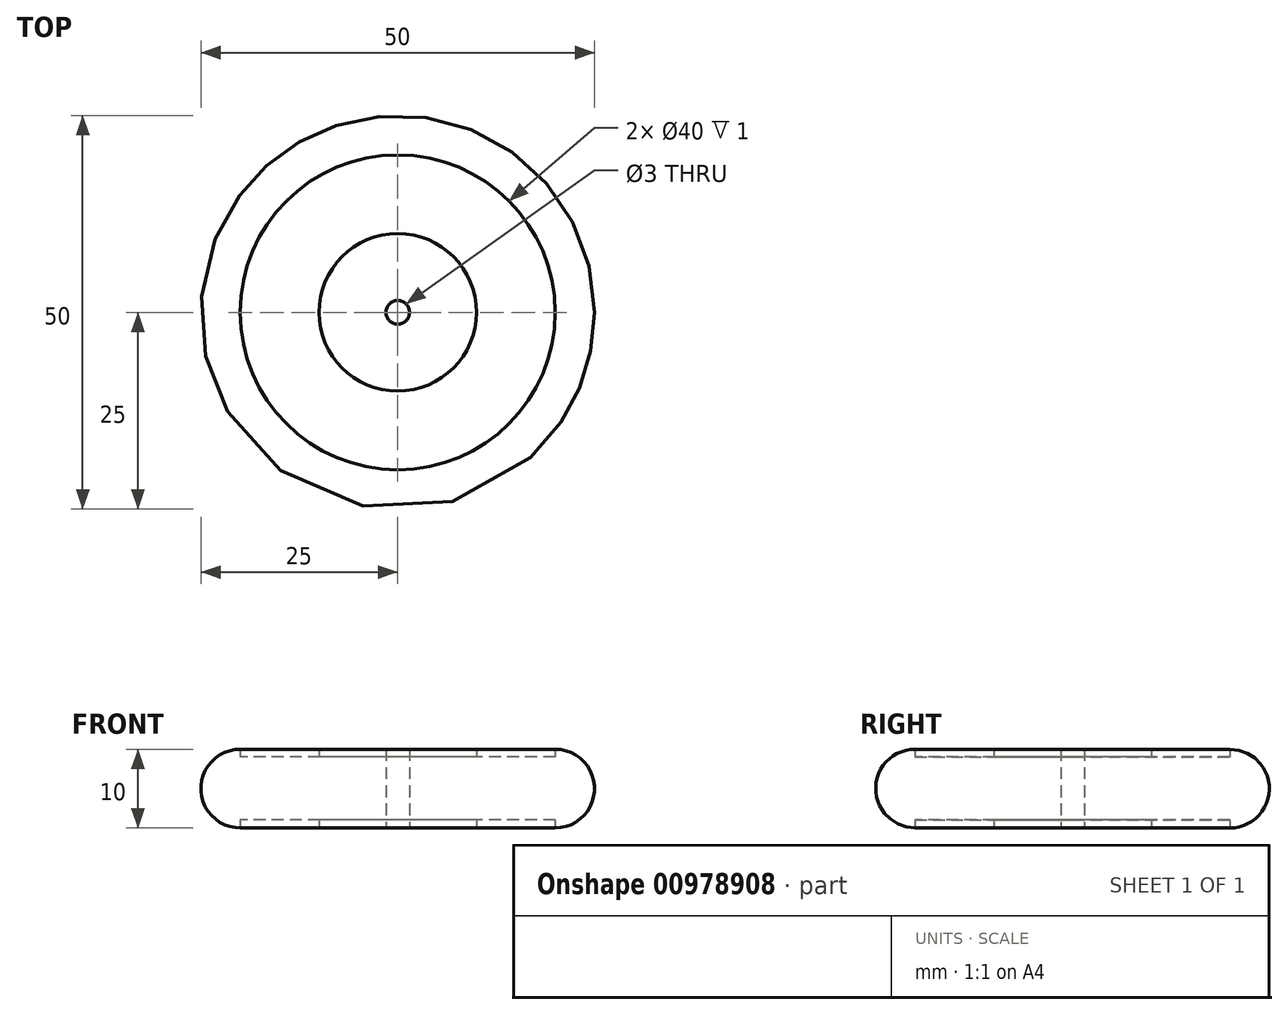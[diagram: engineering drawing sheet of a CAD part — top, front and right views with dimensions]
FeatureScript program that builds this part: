
annotation { "Feature Type Name" : "Feature", "Feature Type Description" : "" }
export const myFeature = defineFeature(function(context is Context, id is Id, definition is map)
    precondition{}
    {
        {
            var Q0;
            Q0=qCreatedBy(makeId("Top.planeOp"),FACE);
            var sketch = newSketch(context, id + "F0", { "sketchPlane" : qUnion([Q0])});
            skCircle(sketch, "E0", {"center": v(0, 0) * mm, "radius": 10 * mm});
            skCircle(sketch, "E1", {"center": v(0, 0) * mm, "radius": 20 * mm});
            skCircle(sketch, "E2", {"center": v(0, 0) * mm, "radius": 25 * mm});
            skSolve(sketch);
        }
        {
            var Q0;
            Q0=makeQuery(id+"F0.imprint","IMPRINT",FACE,{"disambiguationData":[TD([[makeQuery(id+"F0.imprint","IMPRINT",EDGE,{"derivedFrom":sQuery(id+"F0.wireOp",EDGE,"E1")}),-1.0]])]});
            var Q1;
            Q1=makeQuery(id+"F0.imprint","IMPRINT",FACE,{"disambiguationData":[TD([[makeQuery(id+"F0.imprint","IMPRINT",EDGE,{"derivedFrom":sQuery(id+"F0.wireOp",EDGE,"E0")}),1.0]])]});
            extrude(context, id + "F1", {"entities" : qUnion([Q0, Q1]), "endBound" : BoundingType.SYMMETRIC, "depth" : 10 * mm, "offsetDistance" : 25 * mm});
        }
        {
            var Q0;
            Q0=makeQuery(id+"F0.imprint","IMPRINT",FACE,{"disambiguationData":[TD([[makeQuery(id+"F0.imprint","IMPRINT",EDGE,{"derivedFrom":sQuery(id+"F0.wireOp",EDGE,"E0")}),-1.0]])]});
            extrude(context, id + "F2", {"entities" : qUnion([Q0]), "operationType" : NewBodyOperationType.ADD, "endBound" : BoundingType.SYMMETRIC, "depth" : 8 * mm, "offsetDistance" : 25 * mm});
        }
        {
            var Q0;
            Q0=makeQuery(id+"F1.opExtrude","CAP_EDGE",EDGE,{"disambiguationData":[OSD([sQuery(id+"F0.wireOp",EDGE,"E2")])],"isStart":false});
            var Q1;
            Q1=makeQuery(id+"F1.opExtrude","CAP_EDGE",EDGE,{"disambiguationData":[OSD([sQuery(id+"F0.wireOp",EDGE,"E2")])],"isStart":true});
            fillet(context, id + "F3", {"entities" : qUnion([Q0, Q1]), "radius" : 5 * mm, "tangentPropagation" : true, "allowEdgeOverflow" : false});
        }
        {
            var Q0;
            Q0=makeQuery(id+"F1.opExtrude","CAP_FACE",FACE,{"disambiguationData":[OSD([sQuery(id+"F0.wireOp",EDGE,"E0")])],"isStart":true});
            var sketch = newSketch(context, id + "F4", { "sketchPlane" : qUnion([Q0])});
            skPoint(sketch, "E3", {"position": v(0, 0) * mm});
            skSolve(sketch);
        }
        {
            var Q0;
            Q0=sQuery(id+"F4.wireOp",VERTEX,"E3");
            var Q1;
            Q1=makeQuery(id+"F1.opExtrude","SWEPT_BODY",BODY,{"disambiguationData":[OSD([sQuery(id+"F0.wireOp",EDGE,"E0")])]});
            hole(context, id + "F5", {"style" : HoleStyle.SIMPLE, "endStyle" : HoleEndStyle.BLIND, "holeDiameter" : 3 * mm, "majorDiameter" : 5 * mm, "holeDepth" : 250 * mm, "isTappedThrough" : true, "tappedDepth" : 12 * mm, "tapClearance" : 3, "locations" : qUnion([Q0]), "scope" : qUnion([Q1])});
        }
    });
